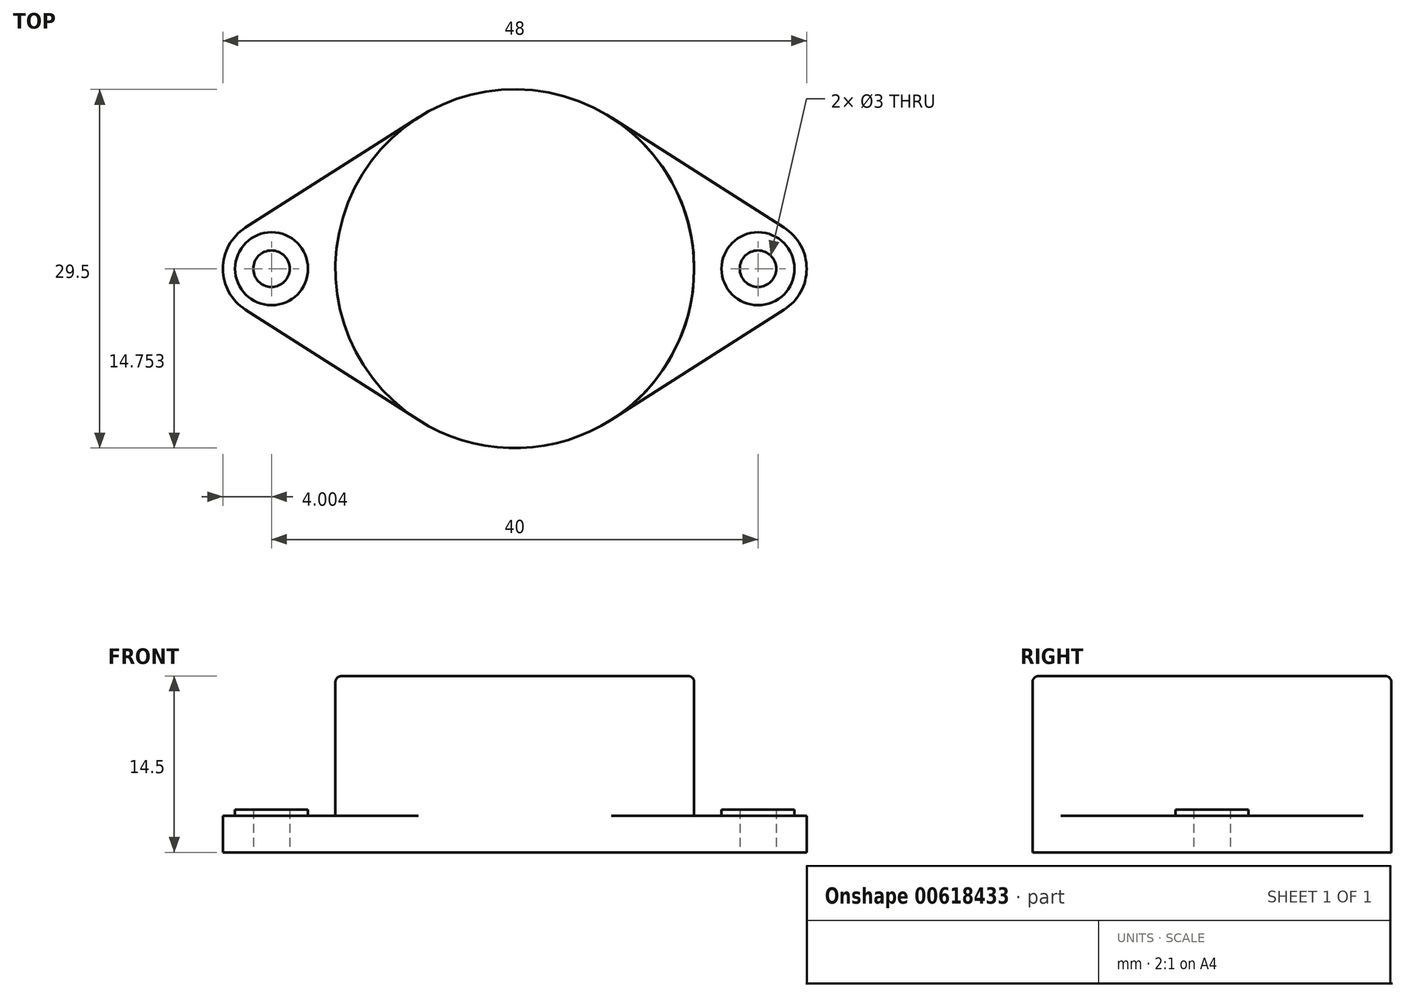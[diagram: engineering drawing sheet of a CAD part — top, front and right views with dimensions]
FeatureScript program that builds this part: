
annotation { "Feature Type Name" : "Feature", "Feature Type Description" : "" }
export const myFeature = defineFeature(function(context is Context, id is Id, definition is map)
    precondition{}
    {
        {
            var Q0;
            Q0=qCreatedBy(makeId("Top.planeOp"),FACE);
            var sketch = newSketch(context, id + "F0", { "sketchPlane" : qUnion([Q0])});
            skCircle(sketch, "E0", {"center": v(-61.02, 16.4) * mm, "radius": 14.75 * mm});
            skCircle(sketch, "E1", {"center": v(-41.02, 16.4) * mm, "radius": 4 * mm});
            skCircle(sketch, "E2", {"center": v(-81.02, 16.4) * mm, "radius": 4 * mm});
            skLineSegment(sketch, "E3", {"start": v(-83.17, 19.77) * mm, "end": v(-68.94, 28.83) * mm});
            skLineSegment(sketch, "E4", {"start": v(-53.09, 28.83) * mm, "end": v(-38.87, 19.77) * mm});
            skLineSegment(sketch, "E5", {"start": v(-38.87, 13.02) * mm, "end": v(-53.09, 3.95) * mm});
            skLineSegment(sketch, "E6", {"start": v(-68.94, 3.95) * mm, "end": v(-83.17, 13.02) * mm});
            skPoint(sketch, "E7.orphan", {"position": v(-62.74, 0) * mm});
            skCircle(sketch, "E8", {"center": v(-41.02, 16.4) * mm, "radius": 3 * mm});
            skCircle(sketch, "E9", {"center": v(-81.02, 16.4) * mm, "radius": 3 * mm});
            skSolve(sketch);
        }
        {
            var Q0;
            {var subQ0=sQuery(id+"F0.wireOp",EDGE,"E0");var subQ1=makeQuery(id+"F0.imprint","INTERSECT",VERTEX,{"derivedFrom":[subQ0,sQuery(id+"F0.wireOp",EDGE,"E3")]});Q0=makeQuery(id+"F0.imprint","IMPRINT",FACE,{"disambiguationData":[TD([[makeQuery(id+"F0.imprint","IMPRINT",EDGE,{"disambiguationData":[TD([[subQ1,1.0]])],"derivedFrom":subQ0}),1.0]])]});}
            var Q1;
            {var subQ0=sQuery(id+"F0.wireOp",EDGE,"E3");Q1=makeQuery(id+"F0.imprint","IMPRINT",FACE,{"disambiguationData":[TD([[makeQuery(id+"F0.imprint","IMPRINT",EDGE,{"derivedFrom":subQ0}),-1.0]])]});}
            var Q2;
            {var subQ0=sQuery(id+"F0.wireOp",EDGE,"E4");Q2=makeQuery(id+"F0.imprint","IMPRINT",FACE,{"disambiguationData":[TD([[makeQuery(id+"F0.imprint","IMPRINT",EDGE,{"derivedFrom":subQ0}),-1.0]])]});}
            var Q3;
            Q3=makeQuery(id+"F0.imprint","IMPRINT",FACE,{"disambiguationData":[TD([[makeQuery(id+"F0.imprint","IMPRINT",EDGE,{"derivedFrom":sQuery(id+"F0.wireOp",EDGE,"E8")}),-1.0]])]});
            var Q4;
            Q4=makeQuery(id+"F0.imprint","IMPRINT",FACE,{"disambiguationData":[TD([[makeQuery(id+"F0.imprint","IMPRINT",EDGE,{"derivedFrom":sQuery(id+"F0.wireOp",EDGE,"E9")}),-1.0]])]});
            extrude(context, id + "F1", {"entities" : qUnion([Q0, Q1, Q2, Q3, Q4]), "depth" : 3 * mm, "offsetDistance" : 25 * mm});
        }
        {
            var Q0;
            Q0=makeQuery(id+"F1.opExtrude","CAP_FACE",FACE,{"disambiguationData":[OSD([sQuery(id+"F0.wireOp",EDGE,"E0"),sQuery(id+"F0.wireOp",EDGE,"E1"),sQuery(id+"F0.wireOp",EDGE,"E2"),sQuery(id+"F0.wireOp",EDGE,"E3"),sQuery(id+"F0.wireOp",EDGE,"E4"),sQuery(id+"F0.wireOp",EDGE,"E5"),sQuery(id+"F0.wireOp",EDGE,"E6")])],"isStart":false});
            var sketch = newSketch(context, id + "F2", { "sketchPlane" : qUnion([Q0])});
            skCircle(sketch, "E10", {"center": v(-61.02, 16.4) * mm, "radius": 14.75 * mm});
            skSolve(sketch);
        }
        {
            var Q0;
            {var subQ0=sQuery(id+"F2.wireOp",EDGE,"E10");var subQ1=makeQuery(id+"F2.imprint","INTERSECT",VERTEX,{"derivedFrom":[makeQuery(id+"F1.opExtrude","CAP_EDGE",EDGE,{"disambiguationData":[OSD([sQuery(id+"F0.wireOp",EDGE,"E3")])],"isStart":false}),subQ0]});Q0=makeQuery(id+"F2.imprint","IMPRINT",FACE,{"disambiguationData":[TD([[makeQuery(id+"F2.imprint","IMPRINT",EDGE,{"disambiguationData":[TD([[subQ1,1.0]])],"derivedFrom":subQ0}),1.0]])]});}
            extrude(context, id + "F3", {"entities" : qUnion([Q0]), "operationType" : NewBodyOperationType.ADD, "depth" : 11.5 * mm, "offsetDistance" : 25 * mm});
        }
        {
            var Q0;
            Q0=makeQuery(id+"F3.opExtrude","CAP_EDGE",EDGE,{"disambiguationData":[OSD([sQuery(id+"F2.wireOp",EDGE,"E10")])],"isStart":false});
            fillet(context, id + "F4", {"entities" : qUnion([Q0]), "radius" : 0.5 * mm, "tangentPropagation" : true, "allowEdgeOverflow" : false});
        }
        {
            var Q0;
            Q0=makeQuery(id+"F1.opExtrude","CAP_FACE",FACE,{"disambiguationData":[OSD([sQuery(id+"F0.wireOp",EDGE,"E0"),sQuery(id+"F0.wireOp",EDGE,"E1"),sQuery(id+"F0.wireOp",EDGE,"E2"),sQuery(id+"F0.wireOp",EDGE,"E3"),sQuery(id+"F0.wireOp",EDGE,"E4"),sQuery(id+"F0.wireOp",EDGE,"E5"),sQuery(id+"F0.wireOp",EDGE,"E6")])],"isStart":true});
            var sketch = newSketch(context, id + "F5", { "sketchPlane" : qUnion([Q0])});
            skPoint(sketch, "E11", {"position": v(-41.02, -16.4) * mm});
            skPoint(sketch, "E12", {"position": v(-81.02, -16.4) * mm});
            skSolve(sketch);
        }
        {
            var Q0;
            Q0=makeQuery(id+"F0.imprint","IMPRINT",FACE,{"disambiguationData":[TD([[makeQuery(id+"F0.imprint","IMPRINT",EDGE,{"derivedFrom":sQuery(id+"F0.wireOp",EDGE,"E8")}),1.0]])]});
            var Q1;
            Q1=makeQuery(id+"F0.imprint","IMPRINT",FACE,{"disambiguationData":[TD([[makeQuery(id+"F0.imprint","IMPRINT",EDGE,{"derivedFrom":sQuery(id+"F0.wireOp",EDGE,"E9")}),1.0]])]});
            extrude(context, id + "F6", {"entities" : qUnion([Q0, Q1]), "operationType" : NewBodyOperationType.ADD, "depth" : 3.5 * mm, "offsetDistance" : 25 * mm});
        }
        {
            var Q0;
            Q0=sQuery(id+"F5.wireOp",VERTEX,"E12");
            var Q1;
            Q1=sQuery(id+"F5.wireOp",VERTEX,"E11");
            var Q2;
            Q2=makeQuery(id+"F1.opExtrude","SWEPT_BODY",BODY,{"disambiguationData":[OSD([sQuery(id+"F0.wireOp",EDGE,"E0"),sQuery(id+"F0.wireOp",EDGE,"E1"),sQuery(id+"F0.wireOp",EDGE,"E2"),sQuery(id+"F0.wireOp",EDGE,"E3"),sQuery(id+"F0.wireOp",EDGE,"E4"),sQuery(id+"F0.wireOp",EDGE,"E5"),sQuery(id+"F0.wireOp",EDGE,"E6"),sQuery(id+"F0.wireOp",EDGE,"E8"),sQuery(id+"F0.wireOp",EDGE,"E9")])]});
            hole(context, id + "F7", {"style" : HoleStyle.SIMPLE, "endStyle" : HoleEndStyle.THROUGH, "holeDiameter" : 3 * mm, "majorDiameter" : 5 * mm, "isTappedThrough" : true, "tappedDepth" : 12 * mm, "tapClearance" : 3, "locations" : qUnion([Q0, Q1]), "scope" : qUnion([Q2])});
        }
    });
